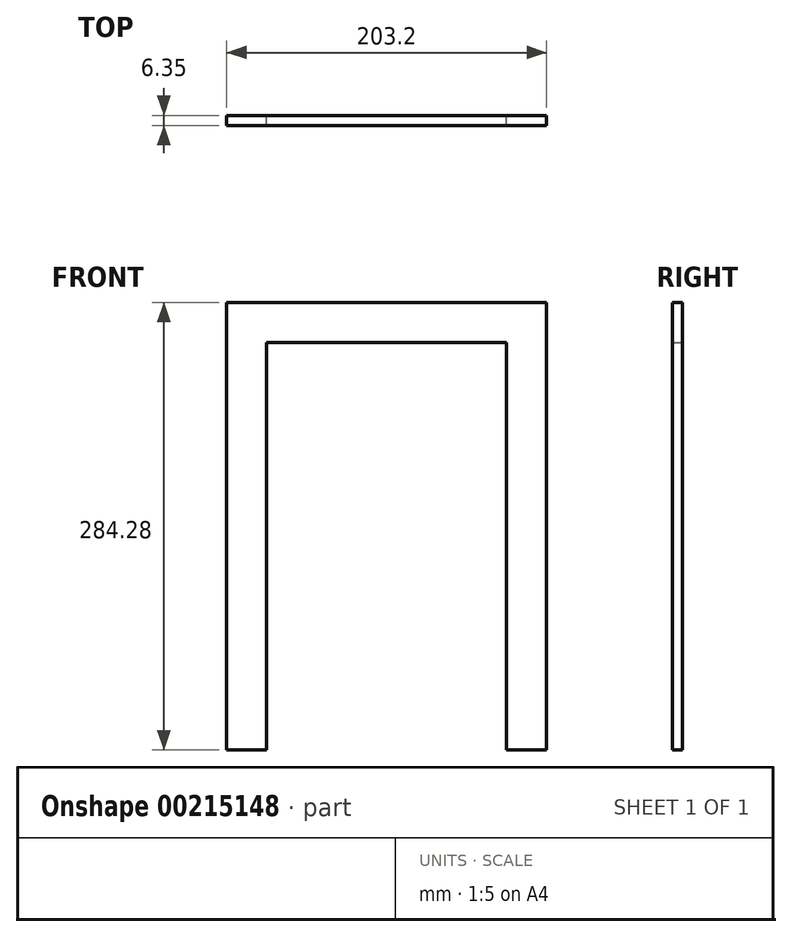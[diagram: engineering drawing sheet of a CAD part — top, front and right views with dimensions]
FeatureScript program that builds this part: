
annotation { "Feature Type Name" : "Feature", "Feature Type Description" : "" }
export const myFeature = defineFeature(function(context is Context, id is Id, definition is map)
    precondition{}
    {
        {
            var Q0;
            Q0=qCreatedBy(makeId("Front.planeOp"),FACE);
            var sketch = newSketch(context, id + "F0", { "sketchPlane" : qUnion([Q0])});
            skLineSegment(sketch, "E0.bottom", {"start": v(101.6, -142.14) * mm, "end": v(-101.6, -142.14) * mm});
            skLineSegment(sketch, "E0.top", {"start": v(101.6, 142.14) * mm, "end": v(-101.6, 142.14) * mm});
            skLineSegment(sketch, "E0.left", {"start": v(101.6, -142.14) * mm, "end": v(101.6, 142.14) * mm});
            skLineSegment(sketch, "E0.right", {"start": v(-101.6, -142.14) * mm, "end": v(-101.6, 142.14) * mm});
            skPoint(sketch, "E0.middle", {"position": v(0, 0) * mm});
            skLineSegment(sketch, "E1", {"start": v(-76.2, -142.14) * mm, "end": v(-76.2, 116.74) * mm});
            skLineSegment(sketch, "E2", {"start": v(-76.2, 116.74) * mm, "end": v(76.2, 116.74) * mm});
            skLineSegment(sketch, "E3", {"start": v(76.2, 116.74) * mm, "end": v(76.2, -142.14) * mm});
            skSolve(sketch);
        }
        {
            var Q0;
            Q0=makeQuery(id+"F0.imprint","IMPRINT",FACE,{"disambiguationData":[TD([[makeQuery(id+"F0.imprint","IMPRINT",EDGE,{"derivedFrom":sQuery(id+"F0.wireOp",EDGE,"E0.top")}),1.0]])]});
            extrude(context, id + "F1", {"entities" : qUnion([Q0]), "depth" : 6.35 * mm});
        }
    });
